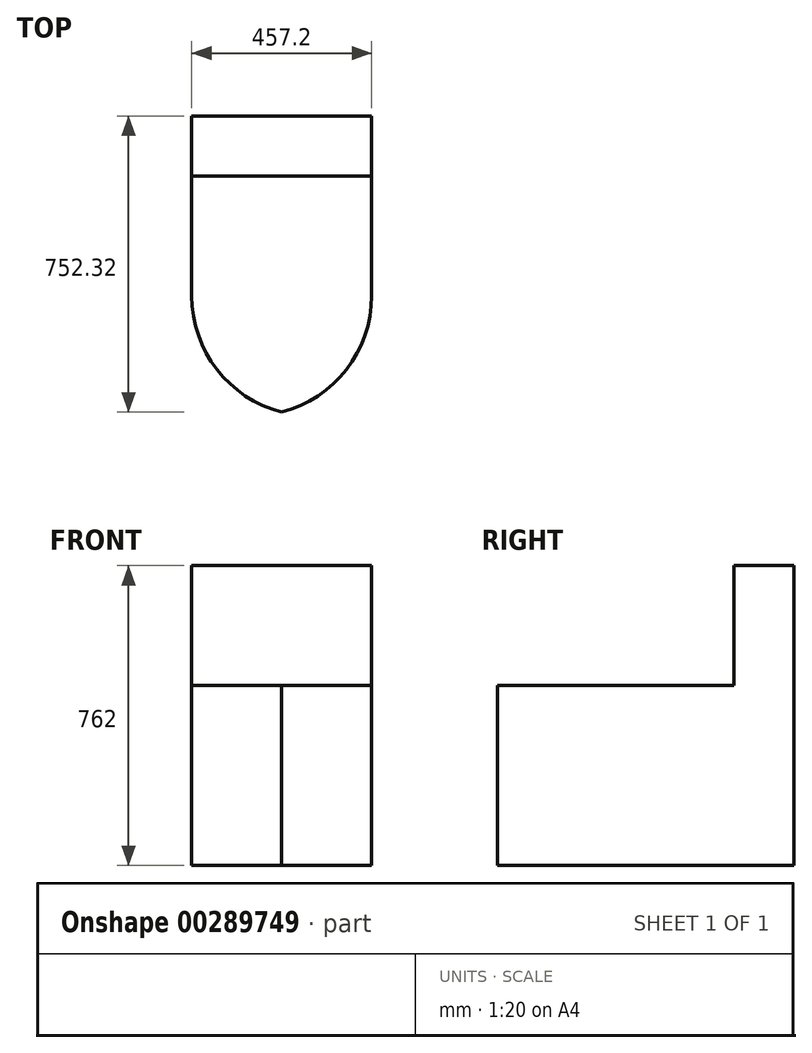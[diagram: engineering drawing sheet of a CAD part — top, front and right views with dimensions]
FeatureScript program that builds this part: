
annotation { "Feature Type Name" : "Feature", "Feature Type Description" : "" }
export const myFeature = defineFeature(function(context is Context, id is Id, definition is map)
    precondition{}
    {
        {
            var Q0;
            Q0=qCreatedBy(makeId("Front.planeOp"),FACE);
            var sketch = newSketch(context, id + "F0", { "sketchPlane" : qUnion([Q0])});
            skLineSegment(sketch, "E0.bottom", {"start": v(228.6, -381) * mm, "end": v(-228.6, -381) * mm});
            skLineSegment(sketch, "E0.top", {"start": v(228.6, 381) * mm, "end": v(-228.6, 381) * mm});
            skLineSegment(sketch, "E0.left", {"start": v(228.6, -381) * mm, "end": v(228.6, 381) * mm});
            skLineSegment(sketch, "E0.right", {"start": v(-228.6, -381) * mm, "end": v(-228.6, 381) * mm});
            skPoint(sketch, "E0.middle", {"position": v(0, 0) * mm});
            skSolve(sketch);
        }
        {
            var Q0;
            Q0=makeQuery(id+"F0.imprint","IMPRINT",FACE,{"disambiguationData":[TD([[makeQuery(id+"F0.imprint","IMPRINT",EDGE,{"derivedFrom":sQuery(id+"F0.wireOp",EDGE,"E0.bottom")}),-1.0]])]});
            extrude(context, id + "F1", {"entities" : qUnion([Q0]), "depth" : 762 * mm, "offsetDistance" : 30.48 * mm});
        }
        {
            var Q0;
            Q0=makeQuery(id+"F1.opExtrude","CAP_FACE",FACE,{"disambiguationData":[OSD([sQuery(id+"F0.wireOp",EDGE,"E0.bottom"),sQuery(id+"F0.wireOp",EDGE,"E0.top"),sQuery(id+"F0.wireOp",EDGE,"E0.left"),sQuery(id+"F0.wireOp",EDGE,"E0.right")])],"isStart":false});
            var sketch = newSketch(context, id + "F2", { "sketchPlane" : qUnion([Q0])});
            skLineSegment(sketch, "E1.bottom", {"start": v(-228.6, 381) * mm, "end": v(228.6, 381) * mm});
            skLineSegment(sketch, "E1.top", {"start": v(-228.6, 76.2) * mm, "end": v(228.6, 76.2) * mm});
            skLineSegment(sketch, "E1.left", {"start": v(-228.6, 381) * mm, "end": v(-228.6, 76.2) * mm});
            skLineSegment(sketch, "E1.right", {"start": v(228.6, 381) * mm, "end": v(228.6, 76.2) * mm});
            skSolve(sketch);
        }
        {
            var Q0;
            Q0=makeQuery(id+"F2.imprint","IMPRINT",FACE,{"disambiguationData":[TD([[makeQuery(id+"F2.imprint","IMPRINT",EDGE,{"derivedFrom":sQuery(id+"F2.wireOp",EDGE,"E1.bottom")}),1.0]])]});
            extrude(context, id + "F3", {"entities" : qUnion([Q0]), "operationType" : NewBodyOperationType.REMOVE, "oppositeDirection" : true, "depth" : 609.6 * mm, "offsetDistance" : 30.48 * mm});
        }
        {
            var Q0;
            Q0=makeQuery(id+"F1.opExtrude","CAP_EDGE",EDGE,{"disambiguationData":[OSD([sQuery(id+"F0.wireOp",EDGE,"E0.right")])],"isStart":false});
            var Q1;
            Q1=makeQuery(id+"F1.opExtrude","CAP_EDGE",EDGE,{"disambiguationData":[OSD([sQuery(id+"F0.wireOp",EDGE,"E0.left")])],"isStart":false});
            fillet(context, id + "F4", {"entities" : qUnion([Q0, Q1]), "tangentPropagation" : true, "radius" : 304.8 * mm, "defaultsChanged" : true, "vertexSettings" : [], "allowEdgeOverflow" : false});
        }
    });
